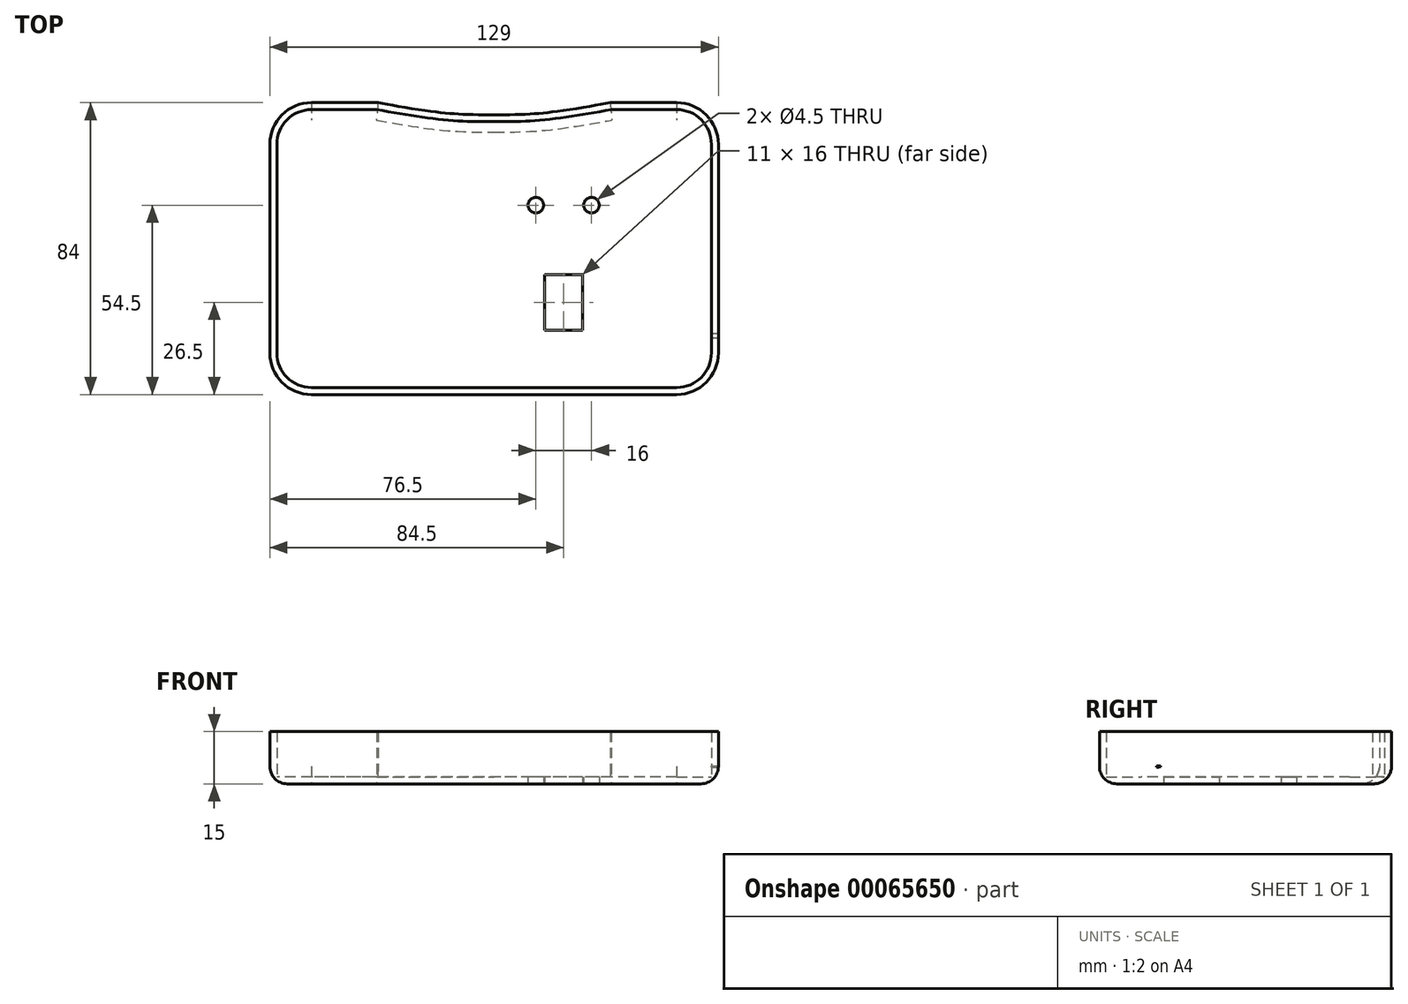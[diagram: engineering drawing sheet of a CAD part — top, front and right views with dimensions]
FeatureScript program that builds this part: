
annotation { "Feature Type Name" : "Feature", "Feature Type Description" : "" }
export const myFeature = defineFeature(function(context is Context, id is Id, definition is map)
    precondition{}
    {
        {
            var Q0;
            Q0=qCreatedBy(makeId("Top.planeOp"),FACE);
            var sketch = newSketch(context, id + "F0", { "sketchPlane" : qUnion([Q0])});
            skLineSegment(sketch, "E0.rect.bottom", {"start": v(52.5, 40) * mm, "end": v(33.75, 40) * mm});
            skLineSegment(sketch, "E0.rect.top", {"start": v(52.5, -40) * mm, "end": v(-52.5, -40) * mm});
            skLineSegment(sketch, "E0.rect.left", {"start": v(62.5, 30) * mm, "end": v(62.5, -30) * mm});
            skLineSegment(sketch, "E0.rect.right", {"start": v(-62.5, 30) * mm, "end": v(-62.5, -30) * mm});
            skPoint(sketch, "E0.rect.middle", {"position": v(0, 0) * mm});
            skPoint(sketch, "E1.visualSharp", {"position": v(-62.5, 40) * mm});
            skArc(sketch, "E1.filletArc", {"start": v(-52.5, 40) * mm, "mid": v(-59.57, 37.07) * mm, "end": v(-62.5, 30) * mm});
            skPoint(sketch, "E2.visualSharp", {"position": v(-62.5, -40) * mm});
            skArc(sketch, "E2.filletArc", {"start": v(-62.5, -30) * mm, "mid": v(-59.57, -37.07) * mm, "end": v(-52.5, -40) * mm});
            skPoint(sketch, "E3.visualSharp", {"position": v(62.5, -40) * mm});
            skArc(sketch, "E3.filletArc", {"start": v(52.5, -40) * mm, "mid": v(59.57, -37.07) * mm, "end": v(62.5, -30) * mm});
            skPoint(sketch, "E4.visualSharp", {"position": v(62.5, 40) * mm});
            skArc(sketch, "E4.filletArc", {"start": v(62.5, 30) * mm, "mid": v(59.57, 37.07) * mm, "end": v(52.5, 40) * mm});
            skArc(sketch, "E5.1", {"start": v(64.5, 30) * mm, "mid": v(60.99, 38.49) * mm, "end": v(52.5, 42) * mm});
            skArc(sketch, "E5.2", {"start": v(-52.5, 42) * mm, "mid": v(-60.99, 38.49) * mm, "end": v(-64.5, 30) * mm});
            skLineSegment(sketch, "E5.3", {"start": v(64.5, 30) * mm, "end": v(64.5, -30) * mm});
            skLineSegment(sketch, "E5.4", {"start": v(-64.5, 30) * mm, "end": v(-64.5, -30) * mm});
            skArc(sketch, "E5.5", {"start": v(-64.5, -30) * mm, "mid": v(-60.99, -38.49) * mm, "end": v(-52.5, -42) * mm});
            skLineSegment(sketch, "E5.6", {"start": v(52.5, -42) * mm, "end": v(-52.5, -42) * mm});
            skArc(sketch, "E5.7", {"start": v(52.5, -42) * mm, "mid": v(60.99, -38.49) * mm, "end": v(64.5, -30) * mm});
            skFitSpline(sketch, "E6", {"points": [v(33.75, 40) * mm, v(13.69, 36.99) * mm, v(0, 36.53) * mm], "startDerivative": vector(-38.24, -6.72) * mm, "endDerivative": vector(-28.95, 0) * mm});
            skFitSpline(sketch, "E7.MirrorCS", {"points": [v(-33.75, 40) * mm, v(-13.69, 36.99) * mm, v(0, 36.53) * mm], "startDerivative": vector(38.24, -6.72) * mm, "endDerivative": vector(28.95, 0) * mm});
            skFitSpline(sketch, "E8.0", {"points": [v(33.4, 41.97) * mm, v(30.22, 41.4) * mm, v(25.45, 40.57) * mm, v(19.4, 39.65) * mm, v(15.79, 39.2) * mm, v(13.06, 38.93) * mm, v(10.42, 38.73) * mm, v(7.26, 38.59) * mm, v(3.6, 38.53) * mm, v(1.2, 38.53) * mm, v(0, 38.53) * mm]});
            skFitSpline(sketch, "E8.1", {"points": [v(-33.4, 41.97) * mm, v(-30.22, 41.4) * mm, v(-25.45, 40.57) * mm, v(-19.4, 39.65) * mm, v(-15.79, 39.2) * mm, v(-13.06, 38.93) * mm, v(-10.42, 38.73) * mm, v(-7.26, 38.59) * mm, v(-3.6, 38.53) * mm, v(-1.2, 38.53) * mm, v(0, 38.53) * mm]});
            skLineSegment(sketch, "E9.trimOffspring", {"start": v(-33.75, 40) * mm, "end": v(-52.5, 40) * mm});
            skLineSegment(sketch, "E10", {"start": v(-52.5, 42) * mm, "end": v(-33.4, 41.97) * mm});
            skLineSegment(sketch, "E11", {"start": v(33.4, 41.97) * mm, "end": v(52.5, 42) * mm});
            skSolve(sketch);
        }
        {
            var Q0;
            Q0=makeQuery(id+"F0.imprint","IMPRINT",FACE,{"disambiguationData":[TD([[makeQuery(id+"F0.imprint","IMPRINT",EDGE,{"derivedFrom":sQuery(id+"F0.wireOp",EDGE,"E0.rect.bottom")}),1.0]])]});
            extrude(context, id + "F1", {"entities" : qUnion([Q0]), "depth" : 2 * mm});
        }
        {
            var Q0;
            Q0=makeQuery(id+"F0.imprint","IMPRINT",FACE,{"disambiguationData":[TD([[makeQuery(id+"F0.imprint","IMPRINT",EDGE,{"derivedFrom":sQuery(id+"F0.wireOp",EDGE,"E0.rect.bottom")}),-1.0]])]});
            var sketch = newSketch(context, id + "F2", { "sketchPlane" : qUnion([Q0])});
            skSolve(sketch);
        }
        {
            var Q0;
            Q0 = qSketchRegion(id + "F2", true);
            var Q1;
            Q1=makeQuery(id+"F0.imprint","IMPRINT",FACE,{"disambiguationData":[TD([[makeQuery(id+"F0.imprint","IMPRINT",EDGE,{"derivedFrom":sQuery(id+"F0.wireOp",EDGE,"E0.rect.bottom")}),-1.0]])]});
            extrude(context, id + "F3", {"entities" : qUnion([Q0, Q1]), "operationType" : NewBodyOperationType.ADD, "depth" : 15 * mm});
        }
        {
            var Q0;
            Q0=makeQuery(id+"F3.opExtrude","CAP_EDGE",EDGE,{"disambiguationData":[OSD([sQuery(id+"F0.wireOp",EDGE,"E5.7")])],"isStart":true});
            var Q1;
            Q1=makeQuery(id+"F3.opExtrude","CAP_EDGE",EDGE,{"disambiguationData":[OSD([sQuery(id+"F0.wireOp",EDGE,"E5.3")])],"isStart":true});
            var Q2;
            Q2=makeQuery(id+"F3.opExtrude","CAP_EDGE",EDGE,{"disambiguationData":[OSD([sQuery(id+"F0.wireOp",EDGE,"E5.1")])],"isStart":true});
            var Q3;
            Q3=makeQuery(id+"F3.opExtrude","CAP_EDGE",EDGE,{"disambiguationData":[OSD([sQuery(id+"F0.wireOp",EDGE,"E11")])],"isStart":true});
            var Q4;
            Q4=makeQuery(id+"F3.opExtrude","CAP_EDGE",EDGE,{"disambiguationData":[OSD([sQuery(id+"F0.wireOp",EDGE,"E8.0")])],"isStart":true});
            var Q5;
            Q5=makeQuery(id+"F3.opExtrude","CAP_EDGE",EDGE,{"disambiguationData":[OSD([sQuery(id+"F0.wireOp",EDGE,"E8.1")])],"isStart":true});
            var Q6;
            Q6=makeQuery(id+"F3.opExtrude","CAP_EDGE",EDGE,{"disambiguationData":[OSD([sQuery(id+"F0.wireOp",EDGE,"E10")])],"isStart":true});
            var Q7;
            Q7=makeQuery(id+"F3.opExtrude","CAP_EDGE",EDGE,{"disambiguationData":[OSD([sQuery(id+"F0.wireOp",EDGE,"E5.2")])],"isStart":true});
            fillet(context, id + "F4", {"entities" : qUnion([Q0, Q1, Q2, Q3, Q4, Q5, Q6, Q7]), "radius" : 5 * mm, "tangentPropagation" : true, "allowEdgeOverflow" : false});
        }
        {
            var Q0;
            Q0=makeQuery(id+"F0.imprint","IMPRINT",FACE,{"disambiguationData":[TD([[makeQuery(id+"F0.imprint","IMPRINT",EDGE,{"derivedFrom":sQuery(id+"F0.wireOp",EDGE,"E0.rect.bottom")}),1.0]])]});
            var sketch = newSketch(context, id + "F5", { "sketchPlane" : qUnion([Q0])});
            skLineSegment(sketch, "E12", {"start": v(0, 0) * mm, "end": v(14.5, 0) * mm, "construction": true});
            skLineSegment(sketch, "E13", {"start": v(14.5, 0) * mm, "end": v(14.5, -7.5) * mm, "construction": true});
            skLineSegment(sketch, "E14.bottom", {"start": v(14.5, -7.5) * mm, "end": v(25.5, -7.5) * mm});
            skLineSegment(sketch, "E14.top", {"start": v(14.5, -23.5) * mm, "end": v(25.5, -23.5) * mm});
            skLineSegment(sketch, "E14.left", {"start": v(14.5, -7.5) * mm, "end": v(14.5, -23.5) * mm});
            skLineSegment(sketch, "E14.right", {"start": v(25.5, -7.5) * mm, "end": v(25.5, -23.5) * mm});
            skLineSegment(sketch, "E15", {"start": v(20, -7.5) * mm, "end": v(20, 12.5) * mm});
            skLineSegment(sketch, "E16", {"start": v(20, 12.5) * mm, "end": v(28, 12.5) * mm});
            skLineSegment(sketch, "E17", {"start": v(20, 12.5) * mm, "end": v(12, 12.5) * mm});
            skCircle(sketch, "E18", {"center": v(28, 12.5) * mm, "radius": 2.25 * mm});
            skCircle(sketch, "E19", {"center": v(12, 12.5) * mm, "radius": 2.25 * mm});
            skLineSegment(sketch, "E20", {"start": v(25.5, -15.5) * mm, "end": v(25.5, -23.5) * mm, "construction": true});
            skLineSegment(sketch, "E21", {"start": v(25.5, -23.5) * mm, "end": v(105.97, -23.5) * mm, "construction": true});
            skSolve(sketch);
        }
        {
            var Q0;
            Q0 = qSketchRegion(id + "F5", true);
            extrude(context, id + "F6", {"entities" : qUnion([Q0]), "operationType" : NewBodyOperationType.REMOVE, "endBound" : BoundingType.THROUGH_ALL, "depth" : 25 * mm, "hasSecondDirection" : true, "secondDirectionBound" : SecondDirectionBoundingType.THROUGH_ALL, "secondDirectionOppositeDirection" : true, "secondDirectionDepth" : 25 * mm});
        }
        {
            var Q0;
            Q0=makeQuery(id+"F3.opExtrude","SWEPT_FACE",FACE,{"disambiguationData":[OSD([sQuery(id+"F0.wireOp",EDGE,"E5.3")])]});
            var sketch = newSketch(context, id + "F7", { "sketchPlane" : qUnion([Q0])});
            skLineSegment(sketch, "E22", {"start": v(-25.6, 0) * mm, "end": v(-25.6, 8) * mm});
            skCircle(sketch, "E23", {"center": v(-25.6, 8) * mm, "radius": 3.25 * mm});
            skPoint(sketch, "E24.endSnap0", {"position": v(0, 5) * mm});
            skCircle(sketch, "E25.MirrorC", {"center": v(26.26, 15) * mm, "radius": 3.7 * mm});
            skSolve(sketch);
        }
        {
            var Q0;
            {var subQ0=sQuery(id+"F7.wireOp",EDGE,"E23");var subQ1=sQuery(id+"F0.wireOp",EDGE,"E5.3");var subQ2=makeQuery(id+"F4.opFillet","BLEND_EDGE",EDGE,{"blendedFrom":[makeQuery(id+"F3.opExtrude","CAP_EDGE",EDGE,{"disambiguationData":[OSD([subQ1])],"isStart":true}),makeQuery(id+"F3.opExtrude","SWEPT_FACE",FACE,{"disambiguationData":[OSD([subQ1])]})],"blendedInto":[makeQuery(id+"F3.opExtrude","SWEPT_FACE",FACE,{"disambiguationData":[OSD([subQ1])]})]});var subQ3=makeQuery(id+"F7.imprint","INTERSECT",VERTEX,{"disambiguationData":[OD(0.0)],"derivedFrom":[subQ2,subQ0]});Q0=makeQuery(id+"F7.imprint","IMPRINT",FACE,{"disambiguationData":[TD([[makeQuery(id+"F7.imprint","IMPRINT",EDGE,{"disambiguationData":[TD([[subQ3,1.0]])],"derivedFrom":subQ0}),1.0]])]});}
            var Q1;
            {var subQ0=sQuery(id+"F7.wireOp",EDGE,"E25.MirrorC");var subQ1=makeQuery(id+"F3.opExtrude","CAP_EDGE",EDGE,{"disambiguationData":[OSD([sQuery(id+"F0.wireOp",EDGE,"E5.3")])],"isStart":false});var subQ2=makeQuery(id+"F7.imprint","INTERSECT",VERTEX,{"disambiguationData":[OD(0.0)],"derivedFrom":[subQ1,subQ0]});Q1=makeQuery(id+"F7.imprint","IMPRINT",FACE,{"disambiguationData":[TD([[makeQuery(id+"F7.imprint","IMPRINT",EDGE,{"disambiguationData":[TD([[subQ2,-1.0]])],"derivedFrom":subQ0}),-1.0]])]});}
            extrude(context, id + "F8", {"entities" : qUnion([Q0, Q1]), "operationType" : NewBodyOperationType.REMOVE, "oppositeDirection" : true, "depth" : 25 * mm, "hasSecondDirection" : true, "secondDirectionOppositeDirection" : false, "secondDirectionDepth" : 25 * mm});
        }
        {
            var Q0;
            {var subQ0=sQuery(id+"F0.wireOp",EDGE,"E5.3");var subQ1=makeQuery(id+"F4.opFillet","BLEND_EDGE",EDGE,{"blendedFrom":[makeQuery(id+"F3.opExtrude","CAP_EDGE",EDGE,{"disambiguationData":[OSD([subQ0])],"isStart":true}),makeQuery(id+"F3.opExtrude","SWEPT_FACE",FACE,{"disambiguationData":[OSD([subQ0])]})],"blendedInto":[makeQuery(id+"F3.opExtrude","SWEPT_FACE",FACE,{"disambiguationData":[OSD([subQ0])]})]});var subQ2=makeQuery(id+"F7.imprint","INTERSECT",VERTEX,{"derivedFrom":[subQ1,sQuery(id+"F7.wireOp",EDGE,"E22")]});Q0=makeQuery(id+"F8.boolean.opBoolean","COPY",FACE,{"derivedFrom":makeQuery(id+"F8.opExtrude","SWEPT_FACE",FACE,{"disambiguationData":[OSD([subQ0]),TDD([makeQuery(id+"F7.imprint","IMPRINT",EDGE,{"disambiguationData":[TD([[subQ2,1.0]])],"derivedFrom":subQ1}),makeQuery(id+"F7.imprint","IMPRINT",EDGE,{"disambiguationData":[TD([[subQ2,-1.0]])],"derivedFrom":subQ1})])]})});}
            extrude(context, id + "F9", {"entities" : qUnion([Q0]), "operationType" : NewBodyOperationType.REMOVE, "oppositeDirection" : true, "depth" : .2 * mm});
        }
    });
